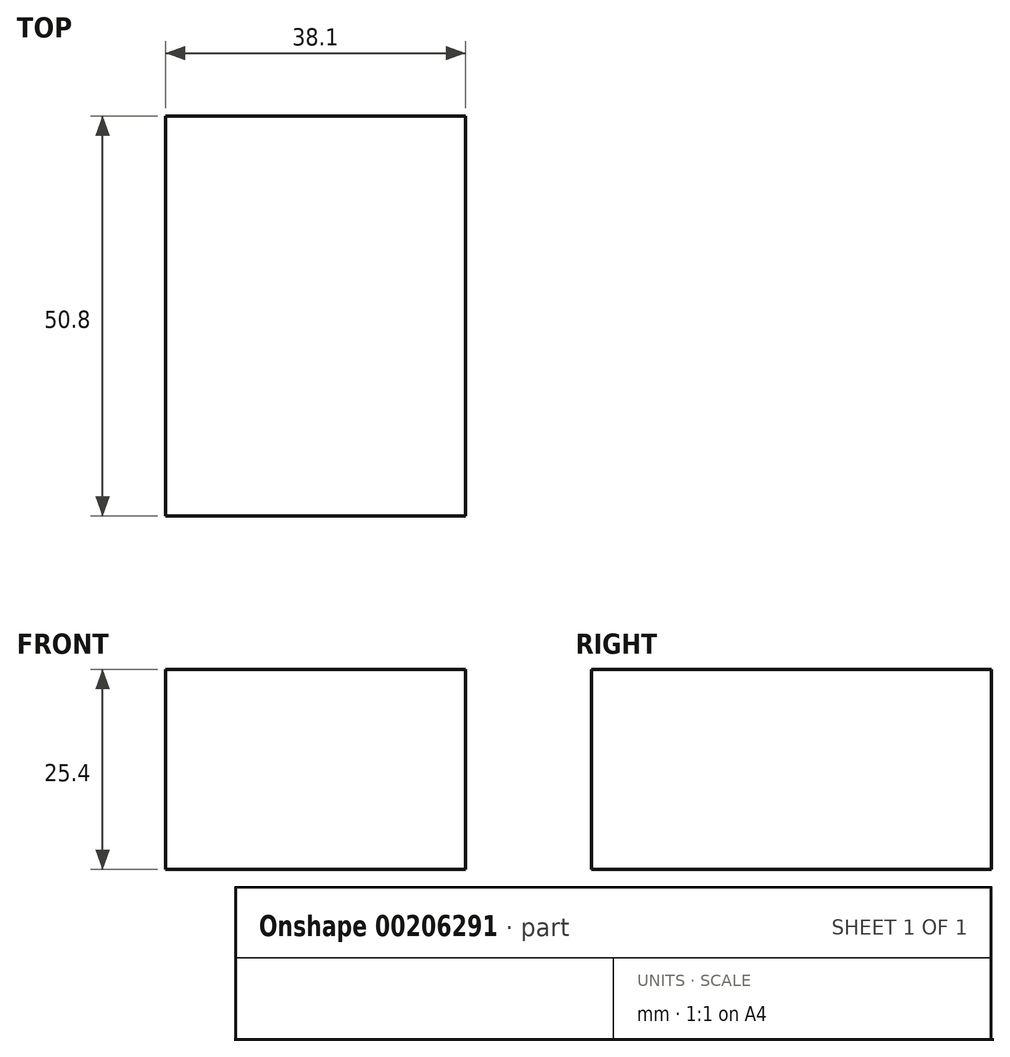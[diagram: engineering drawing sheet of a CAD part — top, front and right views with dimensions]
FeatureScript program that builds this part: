
annotation { "Feature Type Name" : "Feature", "Feature Type Description" : "" }
export const myFeature = defineFeature(function(context is Context, id is Id, definition is map)
    precondition{}
    {
        {
            var Q0;
            Q0=qCreatedBy(makeId("Top.planeOp"),FACE);
            var sketch = newSketch(context, id + "F0", { "sketchPlane" : qUnion([Q0])});
            skLineSegment(sketch, "E0.bottom", {"start": v(0, 0) * mm, "end": v(38.1, 0) * mm});
            skLineSegment(sketch, "E0.top", {"start": v(0, 50.8) * mm, "end": v(38.1, 50.8) * mm});
            skLineSegment(sketch, "E0.left", {"start": v(0, 0) * mm, "end": v(0, 50.8) * mm});
            skLineSegment(sketch, "E0.right", {"start": v(38.1, 0) * mm, "end": v(38.1, 50.8) * mm});
            skSolve(sketch);
        }
        {
            var Q0;
            Q0 = qSketchRegion(id + "F0", true);
            extrude(context, id + "F1", {"entities" : qUnion([Q0]), "depth" : 25.4 * mm});
        }
    });
